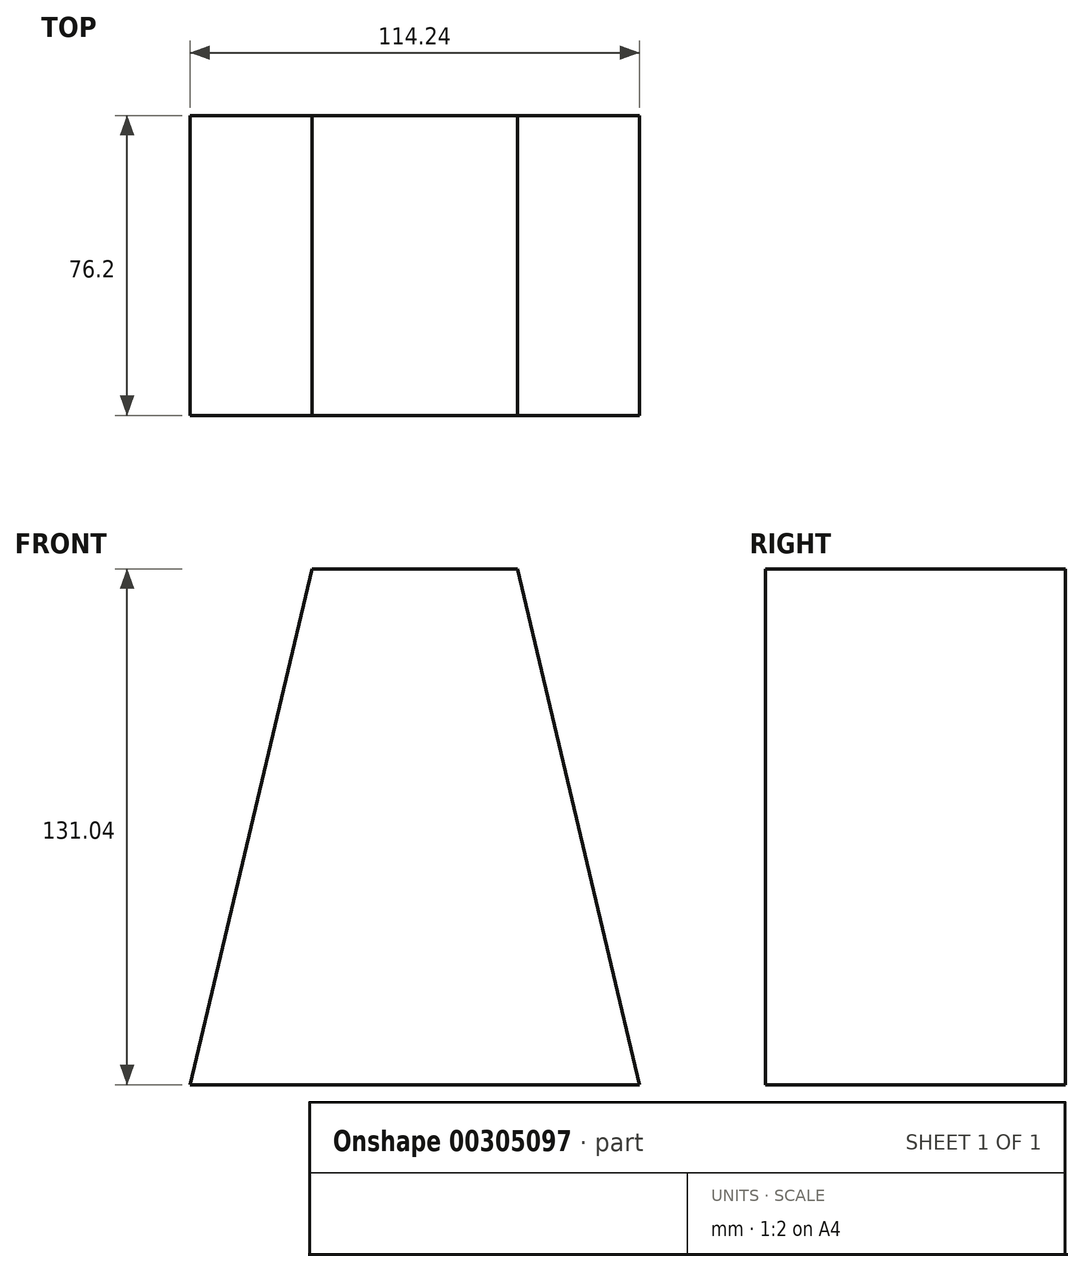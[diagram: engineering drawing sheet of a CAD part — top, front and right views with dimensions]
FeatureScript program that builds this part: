
annotation { "Feature Type Name" : "Feature", "Feature Type Description" : "" }
export const myFeature = defineFeature(function(context is Context, id is Id, definition is map)
    precondition{}
    {
        {
            var Q0;
            Q0=qCreatedBy(makeId("Front.planeOp"),FACE);
            var sketch = newSketch(context, id + "F0", { "sketchPlane" : qUnion([Q0])});
            skLineSegment(sketch, "E0", {"start": v(-31.5, -63.63) * mm, "end": v(82.74, -63.63) * mm});
            skLineSegment(sketch, "E1", {"start": v(82.74, -63.63) * mm, "end": v(51.66, 67.4) * mm});
            skPoint(sketch, "E2", {"position": v(25.62, -63.63) * mm});
            skLineSegment(sketch, "E3.MirrorCS", {"start": v(-31.5, -63.63) * mm, "end": v(-0.42, 67.4) * mm});
            skLineSegment(sketch, "E4", {"start": v(-0.42, 67.4) * mm, "end": v(51.66, 67.4) * mm});
            skSolve(sketch);
        }
        {
            var Q0;
            Q0 = qSketchRegion(id + "F0", true);
            extrude(context, id + "F1", {"entities" : qUnion([Q0]), "depth" : 76.2 * mm});
        }
        {
            var Q0;
            Q0=makeQuery(id+"F1.opExtrude","CAP_FACE",FACE,{"disambiguationData":[OSD([sQuery(id+"F0.wireOp",EDGE,"E0"),sQuery(id+"F0.wireOp",EDGE,"E1"),sQuery(id+"F0.wireOp",EDGE,"E3.MirrorCS"),sQuery(id+"F0.wireOp",EDGE,"E4")])],"isStart":false});
            shell(context, id + "F2", {"entities" : qUnion([Q0]), "thickness" : 101.6 * mm});
        }
    });
